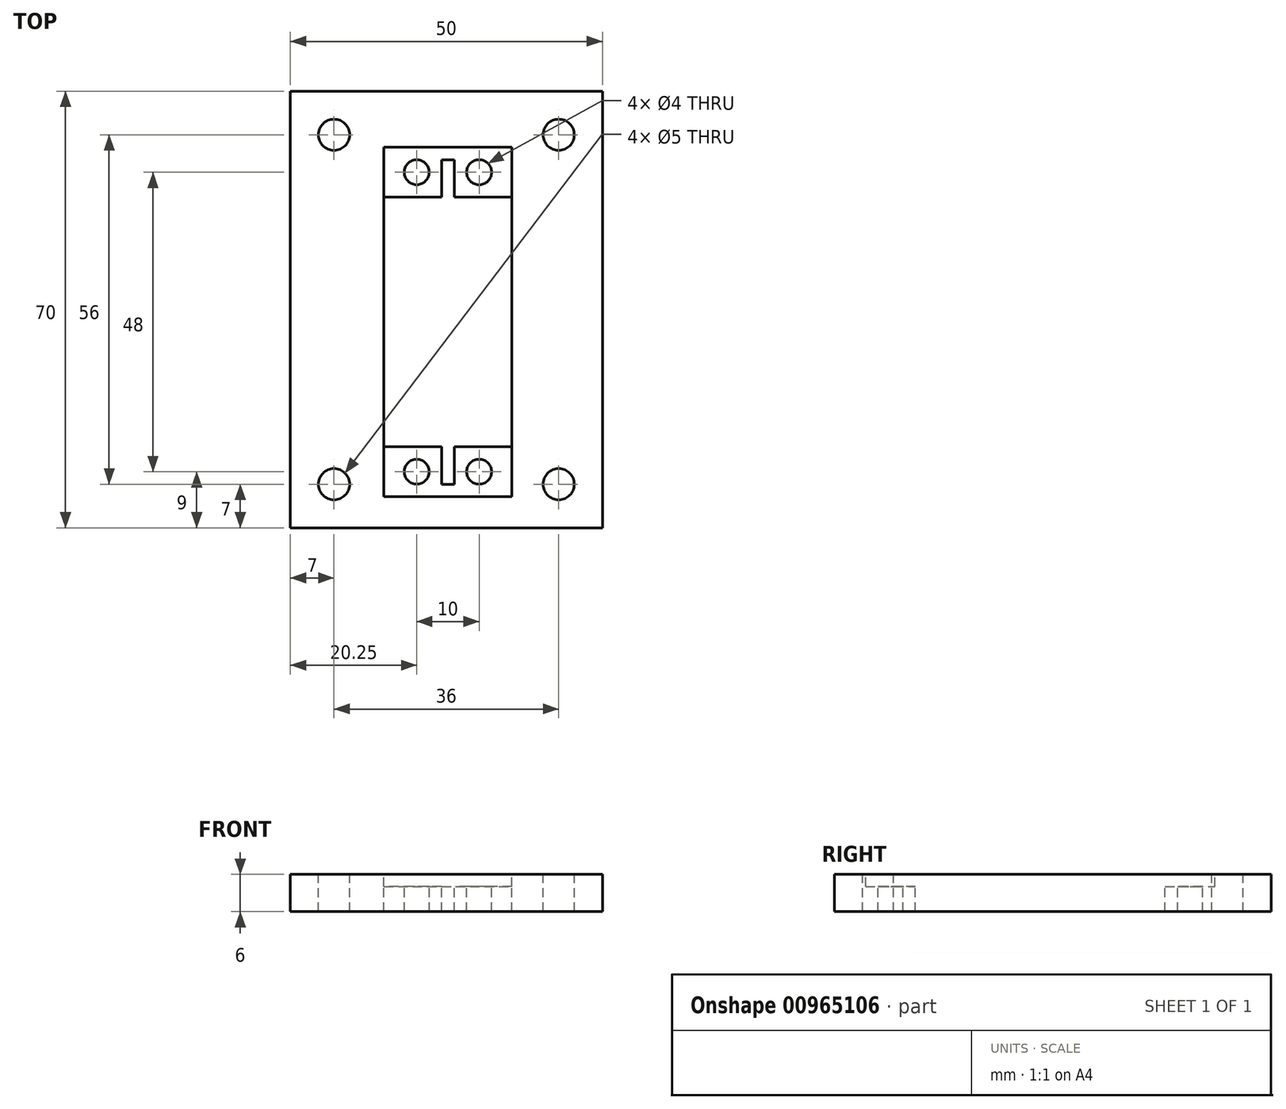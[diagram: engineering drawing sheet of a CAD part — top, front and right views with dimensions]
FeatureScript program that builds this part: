
annotation { "Feature Type Name" : "Feature", "Feature Type Description" : "" }
export const myFeature = defineFeature(function(context is Context, id is Id, definition is map)
    precondition{}
    {
        {
            var Q0;
            Q0=qCreatedBy(makeId("Top.planeOp"),FACE);
            var sketch = newSketch(context, id + "F0", { "sketchPlane" : qUnion([Q0])});
            skLineSegment(sketch, "E0.bottom", {"start": v(0, 0) * mm, "end": v(50, 0) * mm});
            skLineSegment(sketch, "E0.top", {"start": v(0, 70) * mm, "end": v(50, 70) * mm});
            skLineSegment(sketch, "E0.left", {"start": v(0, 0) * mm, "end": v(0, 70) * mm});
            skLineSegment(sketch, "E0.right", {"start": v(50, 0) * mm, "end": v(50, 70) * mm});
            skLineSegment(sketch, "E1.bottom", {"start": v(15, 5) * mm, "end": v(35.5, 5) * mm});
            skLineSegment(sketch, "E1.top", {"start": v(15, 61) * mm, "end": v(35.5, 61) * mm});
            skLineSegment(sketch, "E1.left", {"start": v(15, 5) * mm, "end": v(15, 61) * mm});
            skLineSegment(sketch, "E1.right", {"start": v(35.5, 5) * mm, "end": v(35.5, 61) * mm});
            skLineSegment(sketch, "E2", {"start": v(35.5, 53) * mm, "end": v(15, 53) * mm});
            skLineSegment(sketch, "E3", {"start": v(35.5, 13) * mm, "end": v(15, 13) * mm});
            skCircle(sketch, "E4", {"center": v(20.25, 57) * mm, "radius": 2 * mm});
            skCircle(sketch, "E5", {"center": v(30.25, 57) * mm, "radius": 2 * mm});
            skCircle(sketch, "E6", {"center": v(20.25, 9) * mm, "radius": 2 * mm});
            skCircle(sketch, "E7", {"center": v(30.25, 9) * mm, "radius": 2 * mm});
            skCircle(sketch, "E8", {"center": v(7, 63) * mm, "radius": 2.5 * mm});
            skCircle(sketch, "E9", {"center": v(43, 63) * mm, "radius": 2.5 * mm});
            skCircle(sketch, "E10", {"center": v(7, 7) * mm, "radius": 2.5 * mm});
            skCircle(sketch, "E11", {"center": v(43, 7) * mm, "radius": 2.5 * mm});
            skLineSegment(sketch, "E12.bottom", {"start": v(26.25, 53) * mm, "end": v(24.25, 53) * mm});
            skLineSegment(sketch, "E12.top", {"start": v(26.25, 59) * mm, "end": v(24.25, 59) * mm});
            skLineSegment(sketch, "E12.left", {"start": v(26.25, 53) * mm, "end": v(26.25, 59) * mm});
            skLineSegment(sketch, "E12.right", {"start": v(24.25, 53) * mm, "end": v(24.25, 59) * mm});
            skLineSegment(sketch, "E13.bottom", {"start": v(24.25, 13) * mm, "end": v(26.25, 13) * mm});
            skLineSegment(sketch, "E13.top", {"start": v(24.25, 7) * mm, "end": v(26.25, 7) * mm});
            skLineSegment(sketch, "E13.left", {"start": v(24.25, 13) * mm, "end": v(24.25, 7) * mm});
            skLineSegment(sketch, "E13.right", {"start": v(26.25, 13) * mm, "end": v(26.25, 7) * mm});
            skSolve(sketch);
        }
        {
            var Q0;
            Q0=makeQuery(id+"F0.imprint","IMPRINT",FACE,{"disambiguationData":[TD([[makeQuery(id+"F0.imprint","IMPRINT",EDGE,{"derivedFrom":sQuery(id+"F0.wireOp",EDGE,"E0.bottom")}),1.0]])]});
            var Q1;
            {var subQ2=sQuery(id+"F0.wireOp",EDGE,"E1.top");Q1=makeQuery(id+"F0.imprint","IMPRINT",FACE,{"disambiguationData":[TD([[makeQuery(id+"F0.imprint","IMPRINT",EDGE,{"derivedFrom":subQ2}),-1.0]])]});}
            var Q2;
            {var subQ2=sQuery(id+"F0.wireOp",EDGE,"E1.bottom");Q2=makeQuery(id+"F0.imprint","IMPRINT",FACE,{"disambiguationData":[TD([[makeQuery(id+"F0.imprint","IMPRINT",EDGE,{"derivedFrom":subQ2}),1.0]])]});}
            extrude(context, id + "F1", {"entities" : qUnion([Q0, Q1, Q2]), "oppositeDirection" : true, "depth" : 6 * mm, "offsetDistance" : 25 * mm});
        }
        {
            var Q0;
            {var subQ2=sQuery(id+"F0.wireOp",EDGE,"E1.top");Q0=makeQuery(id+"F0.imprint","IMPRINT",FACE,{"disambiguationData":[TD([[makeQuery(id+"F0.imprint","IMPRINT",EDGE,{"derivedFrom":subQ2}),-1.0]])]});}
            var Q1;
            {var subQ2=sQuery(id+"F0.wireOp",EDGE,"E1.bottom");Q1=makeQuery(id+"F0.imprint","IMPRINT",FACE,{"disambiguationData":[TD([[makeQuery(id+"F0.imprint","IMPRINT",EDGE,{"derivedFrom":subQ2}),1.0]])]});}
            extrude(context, id + "F2", {"entities" : qUnion([Q0, Q1]), "operationType" : NewBodyOperationType.REMOVE, "oppositeDirection" : true, "depth" : 2 * mm, "offsetDistance" : 25 * mm});
        }
    });
